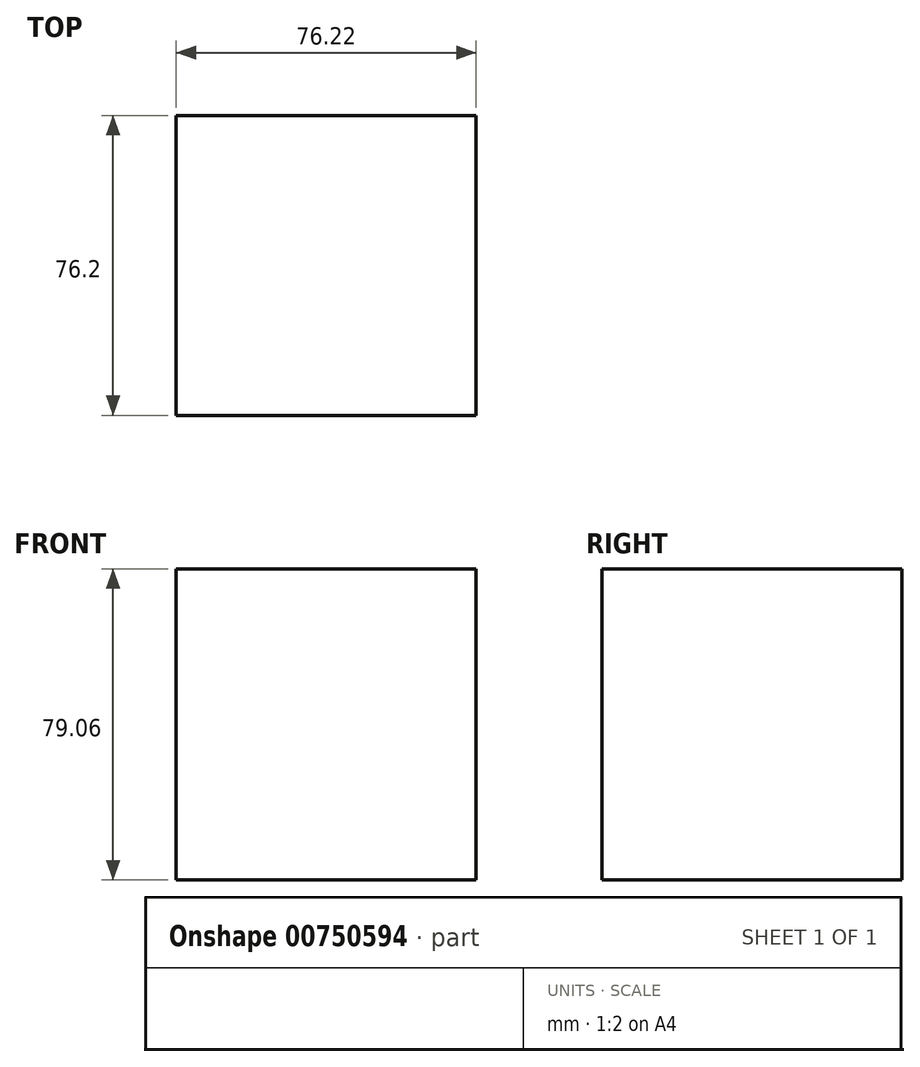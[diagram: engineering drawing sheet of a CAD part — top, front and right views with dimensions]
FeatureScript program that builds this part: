
annotation { "Feature Type Name" : "Feature", "Feature Type Description" : "" }
export const myFeature = defineFeature(function(context is Context, id is Id, definition is map)
    precondition{}
    {
        {
            var Q0;
            Q0=qCreatedBy(makeId("Front.planeOp"),FACE);
            var sketch = newSketch(context, id + "F0", { "sketchPlane" : qUnion([Q0])});
            skLineSegment(sketch, "E0.bottom", {"start": v(-41.8, -42.75) * mm, "end": v(34.41, -42.75) * mm});
            skLineSegment(sketch, "E0.top", {"start": v(-41.8, 36.3) * mm, "end": v(34.41, 36.3) * mm});
            skLineSegment(sketch, "E0.left", {"start": v(-41.8, -42.75) * mm, "end": v(-41.8, 36.3) * mm});
            skLineSegment(sketch, "E0.right", {"start": v(34.41, -42.75) * mm, "end": v(34.41, 36.3) * mm});
            skSolve(sketch);
        }
        {
            var Q0;
            Q0=makeQuery(id+"F0.imprint","IMPRINT",FACE,{"disambiguationData":[TD([[makeQuery(id+"F0.imprint","IMPRINT",EDGE,{"derivedFrom":sQuery(id+"F0.wireOp",EDGE,"E0.bottom")}),1.0]])]});
            extrude(context, id + "F1", {"entities" : qUnion([Q0]), "depth" : 76.2 * mm, "offsetDistance" : 25.4 * mm});
        }
    });
